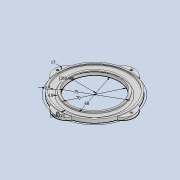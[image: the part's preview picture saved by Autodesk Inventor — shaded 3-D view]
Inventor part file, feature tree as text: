
AUTODESK INVENTOR PART (.ipt)
format: ipt  version: 2020.3 (Build 243373010, 373A)  size: 145,920 bytes
history: native  units: mm
features: extrude x4, sketch x1, hole x1
ambient origin geometry x8: Origin, YZ Plane, XZ Plane, XY Plane, X Axis, Y Axis, Z Axis, Center Point
bodies: Solid1 (feature_tree)
feature tree (6):
  sketch  "Sketch1"  dims[d6=70.0mm d7=68.0mm d8=75.0mm d11=10.0mm d12=2.5mm d13=17.0mm d14=40.0mm d15=40.0mm d17=360.0deg d19=5.0mm d20=0.0mm d21=3.0mm d22=0.0mm d23=4.0mm d24=0.0mm d25=4.0mm d26=0.0mm d27=13.0mm d28=40.0mm d30=360.0deg d32=3.242mm d33=8.0mm d34=4.0mm d35=2.0mm d36=90.0deg d37=11.8mm d38=0.0mm]
  extrude  "Extrusion1"  Depth=2.0mm
  extrude  "Extrusion2"  Depth=2.0mm
  extrude  "Extrusion3"  Depth=10.0mm
  extrude  "Extrusion4"  Depth=2.0mm
  hole  "Hole1"  [1 undecoded]
note: 1 required parameter value undecoded (feature->parameter linkage not recoverable at this tier; creation-order binding heuristic only, values carry confidence <= 0.55)
